# Revit family: Hager-GOLF-Surface_mounted-IP40-With_Cover-With_DIN-Hosted-PL-pl
name_source: partatom
category: Electrical Equipment
units: mm (PartAtom-declared; Revit-internal decimal feet)

## family parameters
Cut with Voids When Loaded = No
Host = Face
Maintain Annotation Orientation = Yes
Panel Configuration = Two Columns, Circuits Across
Part Type = Panelboard
Room Calculation Point = No
Round Connector Dimension = Use Diameter
Shared = No

## types (25) — shared parameters
BC_MODEL_ID = 1539144
BC_OBJECT_ID = 512272
BC_OBJECT_VERSION = #9
Code hager = ADD-EC000214_EU
EF000003 - Sposób montażu = Montaż natynkowy
EF000007 - Kolor = Biały
EF000024 - Odporność na promieniowanie UV = No
EF000049 - Głębokość = 99 mm  [stored 0.324803 ft]
EF000116 - Numer RAL = 9010
EF001062 - Wykonanie zgodne z Dyrektywą Kompatybilności Elektromagnetycznej EMC = No
EF001088 - Możliwość rozbudowy = Yes
EF001134 - Szyna DIN = Yes
EF004462 - Rodzaj zamknięcia = Inne
EF005474 - Stopień ochrony (IP) = IP40
EF006306 - Z zamkiem = No
EF015941 - Drzwi przepuszczające sygnał = Yes
ETIM class code = EC000214
ETIM class name = Small distribution board
HG000001-Number of columns-pl = 1
HG000002-with door or cover-pl = Yes
HG000003-Range-pl = GOLF
HG000005-Thickness-pl = 2 mm  [stored 0.00656168 ft]
HG000006-Flush mounted-pl = No
HG000009-Double swing door-pl = No
HG000010-Asymmetric doors-pl = No
HG000011-Empty rows from bottom-pl = No
HG000012-Door swing angle-pl = 90.00°
HG000013-Door on the left-pl = No
HG000014-Door on the right-pl = Yes
HG000015-Clearance visibility-pl = Yes
HG000016-Door 3D visibility-pl = Yes
HG000017-Distance between poles-pl = 18 mm  [stored 0.0590551 ft]
HG000060-RAL-number = 9010
HG000099-Onfly Template ID-pl-PL = 507532
Manufacturer = Hager
Name = GOLF-Surface_mounted-IP40-With_Cover-With_DIN-PL
Name BIM&CO = Electricity
Name hager = ADD_Enclosures_EC000214
Uniformat = Low Tension Service & Dist.
Uniformat code = D501001
zero-valued in all types: Default Elevation, EF000218 - Głębokość wbudowania, EF000332 - Wysokość wbudowania, EF000846 - Szerokość wbudowania, EF001131 - Głębokość wewnętrzna, HG000007-Number of empty columns-pl, HG000008-Number of empty rows-pl

## per-type parameters (varying)
| type | BC_VARIANT_ID | EF000008 - Szerokość | EF000040 - Wysokość | EF000118 - Z płytą montażową | EF000266 - Liczba rzędów | EF002950 - Szerokość wyrażona liczbą modułów | EF006244 - Transparentna pokrywa/drzwi | EF009212 - Wykonanie/rodzaj pokrywy | EF015776 - Listwa zaciskowa uziemienia | EF015777 - Listwa zaciskowa przewodu neutralnego | HG000004-Manufacturer reference-pl | HGEF000266-Liczba rzędów | HGEF0002950-Szerokość wyrażona liczbą modułów |
| GOLF-Surface_mounted_W138_H184_D99_4_Modular_Spacing-VS104PD | 1169407 | 138 mm  [stored 0.452756 ft] | 184 mm  [stored 0.603675 ft] | No | 1 | 4 | No | Zamknięty | Yes | Yes | VS104PD | 1 | 4 |
| GOLF-Surface_mounted_W138_H184_D99_4_Modular_Spacing-VS104TD | 1169408 | 138 mm  [stored 0.452756 ft] | 184 mm  [stored 0.603675 ft] | No | 1 | 4 | Yes | Zamknięty | Yes | Yes | VS104TD | 1 | 4 |
| GOLF-Surface_mounted_W210_H184_D99_8_Modular_Spacing-VS108PD | 1169409 | 210 mm  [stored 0.688976 ft] | 184 mm  [stored 0.603675 ft] | No | 1 | 8 | No | Zamknięty | Yes | Yes | VS108PD | 1 | 8 |
| GOLF-Surface_mounted_W210_H184_D99_8_Modular_Spacing-VS108TD | 1169410 | 210 mm  [stored 0.688976 ft] | 184 mm  [stored 0.603675 ft] | No | 1 | 8 | Yes | Zamknięty | Yes | Yes | VS108TD | 1 | 8 |
| GOLF-Surface_mounted_W282_H252_D99_12_Modular_Spacing-VS112PD | 1169411 | 282 mm | 252 mm  [stored 0.826772 ft] | No | 1 | 12 | No | Zamknięty | Yes | Yes | VS112PD | 1 | 12 |
| GOLF-Surface_mounted_W282_H252_D99_12_Modular_Spacing-VS112TD | 1169412 | 282 mm | 252 mm  [stored 0.826772 ft] | No | 1 | 12 | Yes | Zamknięty | Yes | Yes | VS112TD | 1 | 12 |
| GOLF-Surface_mounted_W390_H252_D99_18_Modular_Spacing-VS118PD | 1169413 | 390 mm  [stored 1.27953 ft] | 252 mm  [stored 0.826772 ft] | No | 1 | 18 | No | Zamknięty | Yes | Yes | VS118PD | 1 | 18 |
| GOLF-Surface_mounted_W390_H252_D99_18_Modular_Spacing-VS118TD | 1169414 | 390 mm  [stored 1.27953 ft] | 252 mm  [stored 0.826772 ft] | No | 1 | 18 | Yes | Zamknięty | Yes | Yes | VS118TD | 1 | 18 |
| GOLF-Surface_mounted_W462_H252_D99_22_Modular_Spacing-VS122PD | 1169415 | 462 mm  [stored 1.51575 ft] | 252 mm  [stored 0.826772 ft] | No | 1 | 22 | No | Zamknięty | Yes | Yes | VS122PD | 1 | 22 |
| GOLF-Surface_mounted_W462_H252_D99_22_Modular_Spacing-VS122TD | 1169416 | 462 mm  [stored 1.51575 ft] | 252 mm  [stored 0.826772 ft] | No | 1 | 22 | Yes | Zamknięty | Yes | Yes | VS122TD | 1 | 22 |
| GOLF-Surface_mounted_W282_H377_D99_12_Modular_Spacing-VS212PD | 1169417 | 282 mm | 377 mm  [stored 1.23688 ft] | No | 2 | 12 | No | Zamknięty | Yes | Yes | VS212PD | 2 | 12 |
| GOLF-Surface_mounted_W282_H377_D99_12_Modular_Spacing-VS212TD | 1169418 | 282 mm | 377 mm  [stored 1.23688 ft] | No | 2 | 12 | Yes | Zamknięty | Yes | Yes | VS212TD | 2 | 12 |
| GOLF-Surface_mounted_W390_H377_D99_18_Modular_Spacing-VS218PD | 1169419 | 390 mm  [stored 1.27953 ft] | 377 mm  [stored 1.23688 ft] | No | 2 | 18 | No | Zamknięty | Yes | Yes | VS218PD | 2 | 18 |
| GOLF-Surface_mounted_W390_H377_D99_18_Modular_Spacing-VS218PZF | 1169420 | 390 mm  [stored 1.27953 ft] | 377 mm  [stored 1.23688 ft] | Yes | 2 | 18 | No | Z otworem | No | No | VS218PZF | 2 | 18 |
| GOLF-Surface_mounted_W390_H377_D99_18_Modular_Spacing-VS218TD | 1169421 | 390 mm  [stored 1.27953 ft] | 377 mm  [stored 1.23688 ft] | No | 2 | 18 | Yes | Zamknięty | Yes | Yes | VS218TD | 2 | 18 |
| GOLF-Surface_mounted_W282_H500_D99_12_Modular_Spacing-VS312PD | 1169422 | 282 mm | 500 mm  [stored 1.64042 ft] | No | 3 | 12 | No | Zamknięty | Yes | Yes | VS312PD | 3 | 12 |
| GOLF-Surface_mounted_W282_H500_D99_12_Modular_Spacing-VS312TD | 1169423 | 282 mm | 500 mm  [stored 1.64042 ft] | No | 3 | 12 | Yes | Zamknięty | Yes | Yes | VS312TD | 3 | 12 |
| GOLF-Surface_mounted_W390_H500_D99_18_Modular_Spacing-VS318PD | 1169424 | 390 mm  [stored 1.27953 ft] | 500 mm  [stored 1.64042 ft] | No | 3 | 18 | No | Zamknięty | Yes | Yes | VS318PD | 3 | 18 |
| GOLF-Surface_mounted_W390_H500_D99_18_Modular_Spacing-VS318PZF | 1169425 | 390 mm  [stored 1.27953 ft] | 500 mm  [stored 1.64042 ft] | Yes | 3 | 18 | No | Z otworem | No | No | VS318PZF | 3 | 18 |
| GOLF-Surface_mounted_W390_H500_D99_18_Modular_Spacing-VS318TD | 1169426 | 390 mm  [stored 1.27953 ft] | 500 mm  [stored 1.64042 ft] | No | 3 | 18 | Yes | Zamknięty | Yes | Yes | VS318TD | 3 | 18 |
| GOLF-Surface_mounted_W282_H647_D99_12_Modular_Spacing-VS412PD | 1169427 | 282 mm | 647 mm  [stored 2.1227 ft] | No | 4 | 12 | No | Zamknięty | Yes | Yes | VS412PD | 4 | 12 |
| GOLF-Surface_mounted_W282_H647_D99_12_Modular_Spacing-VS412TD | 1169428 | 282 mm | 647 mm  [stored 2.1227 ft] | No | 4 | 12 | Yes | Zamknięty | Yes | Yes | VS412TD | 4 | 12 |
| GOLF-Surface_mounted_W390_H647_D99_18_Modular_Spacing-VS418PD | 1169429 | 390 mm  [stored 1.27953 ft] | 647 mm  [stored 2.1227 ft] | No | 4 | 18 | No | Zamknięty | Yes | Yes | VS418PD | 4 | 18 |
| GOLF-Surface_mounted_W390_H647_D99_18_Modular_Spacing-VS418PZF | 1169430 | 390 mm  [stored 1.27953 ft] | 647 mm  [stored 2.1227 ft] | Yes | 4 | 18 | No | Z otworem | No | No | VS418PZF | 4 | 18 |
| GOLF-Surface_mounted_W390_H647_D99_18_Modular_Spacing-VS418TD | 1169431 | 390 mm  [stored 1.27953 ft] | 647 mm  [stored 2.1227 ft] | No | 4 | 18 | Yes | Zamknięty | Yes | Yes | VS418TD | 4 | 18 |

note: column(s) folded — value = type name in every type: Reference

note: [stored X ft] marks values corroborated as IEEE doubles in the binary element streams (Revit-internal decimal feet)

## geometry (parser evidence)
native form markers: Sweep x14
no freeform markers — native parametric forms only
